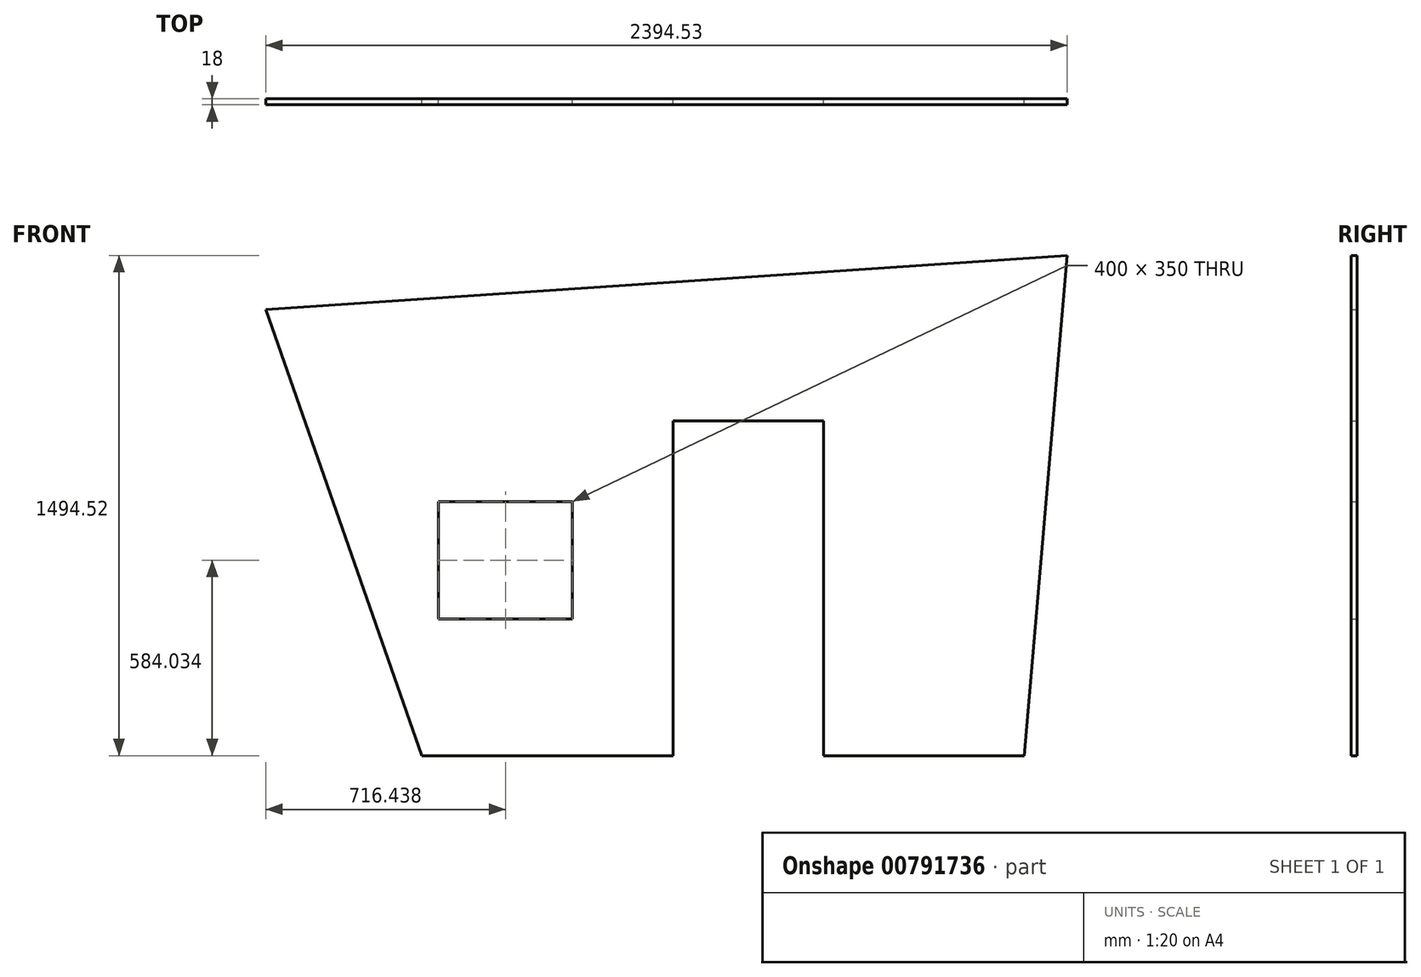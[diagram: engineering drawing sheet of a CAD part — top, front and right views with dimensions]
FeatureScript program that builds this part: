
annotation { "Feature Type Name" : "Feature", "Feature Type Description" : "" }
export const myFeature = defineFeature(function(context is Context, id is Id, definition is map)
    precondition{}
    {
        {
            var Q0;
            Q0=qCreatedBy(makeId("Front.planeOp"),FACE);
            var sketch = newSketch(context, id + "F0", { "sketchPlane" : qUnion([Q0])});
            skLineSegment(sketch, "E0", {"start": v(-833.48, -811.01) * mm, "end": v(966.52, -811.01) * mm});
            skLineSegment(sketch, "E1", {"start": v(966.52, -811.01) * mm, "end": v(1094.61, 683.5) * mm});
            skLineSegment(sketch, "E2", {"start": v(1094.61, 683.5) * mm, "end": v(-1299.92, 521.63) * mm});
            skLineSegment(sketch, "E3", {"start": v(-1299.92, 521.63) * mm, "end": v(-833.48, -811.01) * mm});
            skLineSegment(sketch, "E4", {"start": v(-83.48, -811.01) * mm, "end": v(-83.48, 188.99) * mm});
            skLineSegment(sketch, "E5", {"start": v(-83.48, 188.99) * mm, "end": v(366.52, 188.99) * mm});
            skLineSegment(sketch, "E6", {"start": v(366.52, 188.99) * mm, "end": v(366.52, -811.01) * mm});
            skLineSegment(sketch, "E7.bottom", {"start": v(-783.48, -51.98) * mm, "end": v(-383.48, -51.98) * mm});
            skLineSegment(sketch, "E7.top", {"start": v(-783.48, -401.98) * mm, "end": v(-383.48, -401.98) * mm});
            skLineSegment(sketch, "E7.left", {"start": v(-783.48, -51.98) * mm, "end": v(-783.48, -401.98) * mm});
            skLineSegment(sketch, "E7.right", {"start": v(-383.48, -51.98) * mm, "end": v(-383.48, -401.98) * mm});
            skSolve(sketch);
        }
        {
            var Q0;
            {var subQ4=sQuery(id+"F0.wireOp",EDGE,"E1");Q0=makeQuery(id+"F0.imprint","IMPRINT",FACE,{"disambiguationData":[TD([[makeQuery(id+"F0.imprint","IMPRINT",EDGE,{"derivedFrom":subQ4}),1.0]])]});}
            extrude(context, id + "F1", {"entities" : qUnion([Q0]), "depth" : 18 * mm, "offsetDistance" : 25 * mm});
        }
    });
